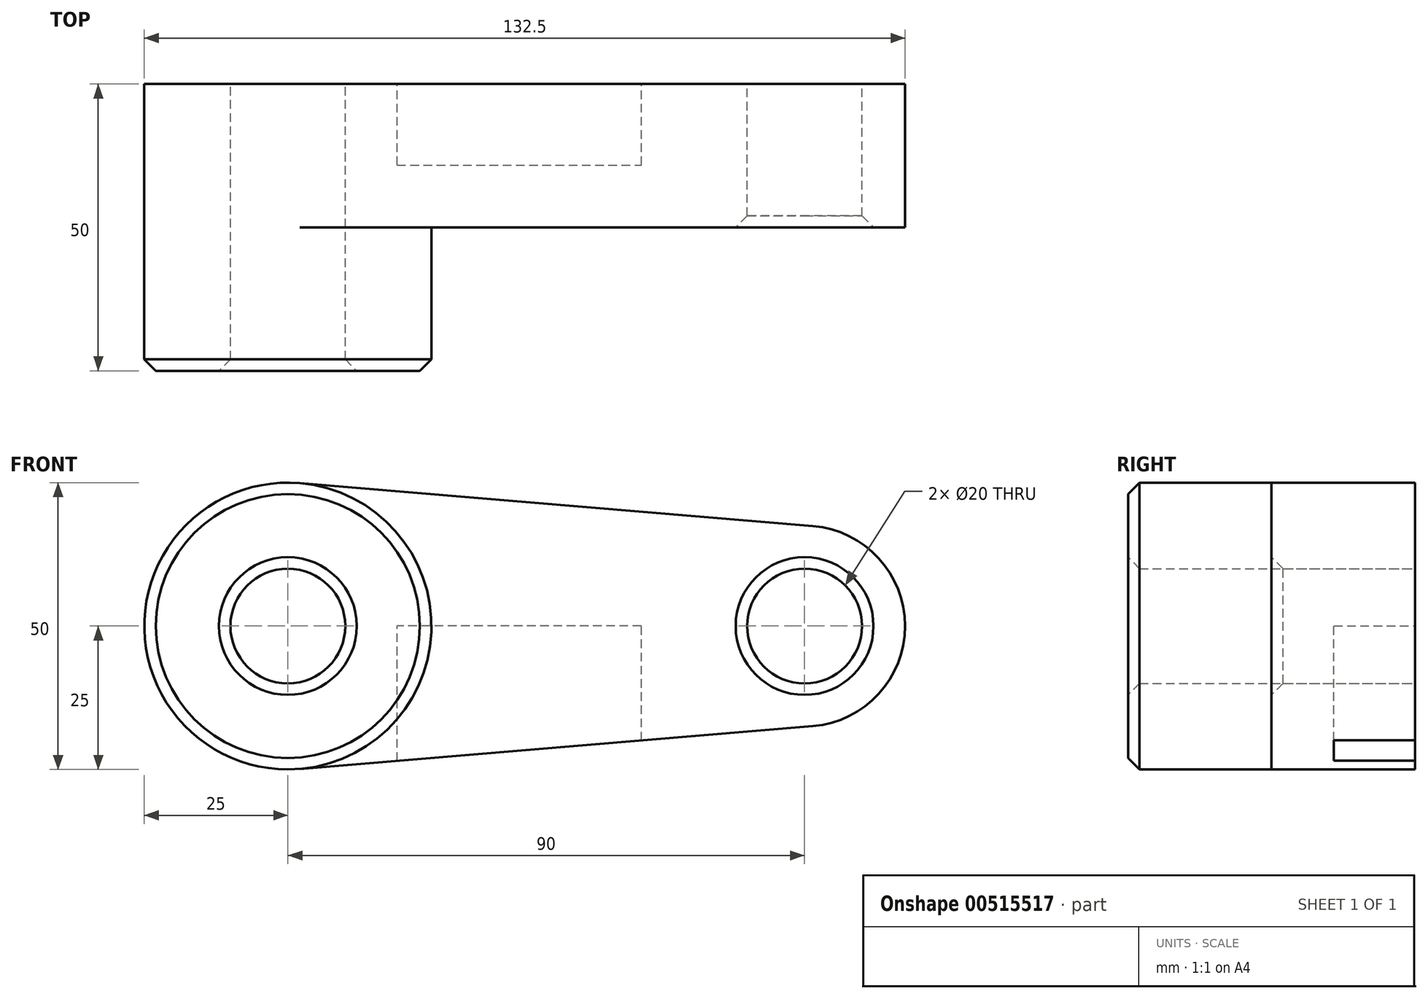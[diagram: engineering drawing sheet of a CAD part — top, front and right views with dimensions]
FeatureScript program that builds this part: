
annotation { "Feature Type Name" : "Feature", "Feature Type Description" : "" }
export const myFeature = defineFeature(function(context is Context, id is Id, definition is map)
    precondition{}
    {
        {
            var Q0;
            Q0=qCreatedBy(makeId("Front.planeOp"),FACE);
            var sketch = newSketch(context, id + "F0", { "sketchPlane" : qUnion([Q0])});
            skCircle(sketch, "E0", {"center": v(0, 0) * mm, "radius": 25 * mm});
            skCircle(sketch, "E1", {"center": v(90, 0) * mm, "radius": 17.5 * mm});
            skLineSegment(sketch, "E2", {"start": v(2.08, 24.91) * mm, "end": v(91.46, 17.44) * mm});
            skLineSegment(sketch, "E3", {"start": v(2.08, -24.91) * mm, "end": v(91.46, -17.44) * mm});
            skCircle(sketch, "E4", {"center": v(0, 0) * mm, "radius": 10 * mm});
            skCircle(sketch, "E5", {"center": v(90, 0) * mm, "radius": 10 * mm});
            skSolve(sketch);
        }
        {
            var Q0;
            Q0=qSketchRegion(id+"F0",true);
            extrude(context, id + "F1", {"entities" : qUnion([Q0]), "depth" : 25 * mm});
        }
        {
            var Q0;
            Q0=makeQuery(id+"F0.imprint","IMPRINT",FACE,{"disambiguationData":[TD([[makeQuery(id+"F0.imprint","IMPRINT",EDGE,{"derivedFrom":sQuery(id+"F0.wireOp",EDGE,"E4")}),-1.0]])]});
            extrude(context, id + "F2", {"entities" : qUnion([Q0]), "operationType" : NewBodyOperationType.ADD, "depth" : 50 * mm});
        }
        {
            var Q0;
            Q0=makeQuery(id+"F2.opExtrude","CAP_EDGE",EDGE,{"disambiguationData":[OSD([sQuery(id+"F0.wireOp",EDGE,"E0")])],"isStart":false});
            var Q1;
            Q1=makeQuery(id+"F2.opExtrude","CAP_EDGE",EDGE,{"disambiguationData":[OSD([sQuery(id+"F0.wireOp",EDGE,"E4")])],"isStart":false});
            var Q2;
            Q2=makeQuery(id+"F1.opExtrude","CAP_EDGE",EDGE,{"disambiguationData":[OSD([sQuery(id+"F0.wireOp",EDGE,"E5")])],"isStart":false});
            chamfer(context, id + "F3", {"entities" : qUnion([Q0, Q1, Q2]), "width" : 2 * mm, "tangentPropagation" : true});
        }
        {
            var Q0;
            Q0=qCreatedBy(makeId("Top.planeOp"),FACE);
            var sketch = newSketch(context, id + "F4", { "sketchPlane" : qUnion([Q0])});
            skLineSegment(sketch, "E6.bottom", {"start": v(19.02, -14.15) * mm, "end": v(61.57, -14.15) * mm});
            skLineSegment(sketch, "E6.top", {"start": v(19.02, 46.03) * mm, "end": v(61.57, 46.03) * mm});
            skLineSegment(sketch, "E6.left", {"start": v(19.02, -14.15) * mm, "end": v(19.02, 46.03) * mm});
            skLineSegment(sketch, "E6.right", {"start": v(61.57, -14.15) * mm, "end": v(61.57, 46.03) * mm});
            skSolve(sketch);
        }
        {
            var Q0;
            Q0=makeQuery(id+"F4.imprint","IMPRINT",FACE,{"disambiguationData":[TD([[makeQuery(id+"F4.imprint","IMPRINT",EDGE,{"derivedFrom":sQuery(id+"F4.wireOp",EDGE,"E6.bottom")}),1.0]])]});
            extrude(context, id + "F5", {"entities" : qUnion([Q0]), "operationType" : NewBodyOperationType.REMOVE, "oppositeDirection" : true, "depth" : 25 * mm, "offsetDistance" : 25 * mm});
        }
    });
